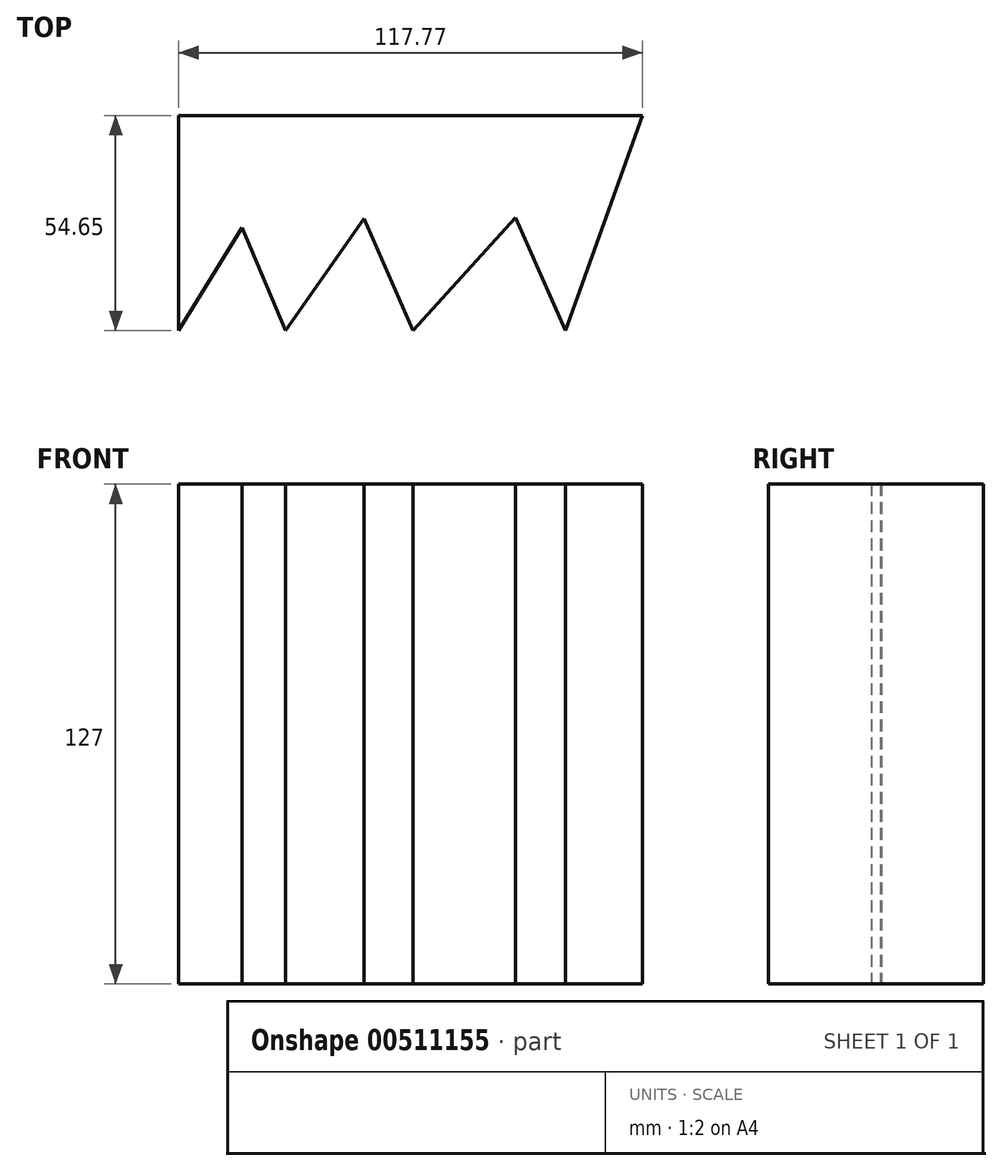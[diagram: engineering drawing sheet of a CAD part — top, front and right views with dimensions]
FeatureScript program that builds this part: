
annotation { "Feature Type Name" : "Feature", "Feature Type Description" : "" }
export const myFeature = defineFeature(function(context is Context, id is Id, definition is map)
    precondition{}
    {
        {
            var Q0;
            Q0=qCreatedBy(makeId("Top.planeOp"),FACE);
            var sketch = newSketch(context, id + "F0", { "sketchPlane" : qUnion([Q0])});
            skLineSegment(sketch, "E0", {"start": v(-59.46, 54.65) * mm, "end": v(58.3, 54.65) * mm});
            skLineSegment(sketch, "E1", {"start": v(58.3, 54.65) * mm, "end": v(38.77, 0) * mm});
            skLineSegment(sketch, "E2", {"start": v(38.77, 0) * mm, "end": v(26.04, 28.72) * mm});
            skLineSegment(sketch, "E3", {"start": v(26.04, 28.72) * mm, "end": v(0, 0) * mm});
            skLineSegment(sketch, "E4", {"start": v(0, 0) * mm, "end": v(-12.43, 28.44) * mm});
            skLineSegment(sketch, "E5", {"start": v(-12.43, 28.44) * mm, "end": v(-32.35, 0) * mm});
            skLineSegment(sketch, "E6", {"start": v(-32.35, 0) * mm, "end": v(-43.42, 26.23) * mm});
            skLineSegment(sketch, "E7", {"start": v(-43.42, 26.23) * mm, "end": v(-59.47, 0) * mm});
            skLineSegment(sketch, "E8", {"start": v(-59.47, 0) * mm, "end": v(-59.46, 54.65) * mm});
            skLineSegment(sketch, "E9", {"start": v(103.24, 44.22) * mm, "end": v(103.24, 40.62) * mm});
            skSolve(sketch);
        }
        {
            var Q0;
            Q0=makeQuery(id+"F0.imprint","IMPRINT",FACE,{"disambiguationData":[TD([[makeQuery(id+"F0.imprint","IMPRINT",EDGE,{"derivedFrom":sQuery(id+"F0.wireOp",EDGE,"E0")}),-1.0]])]});
            extrude(context, id + "F1", {"entities" : qUnion([Q0]), "depth" : 127 * mm});
        }
    });
